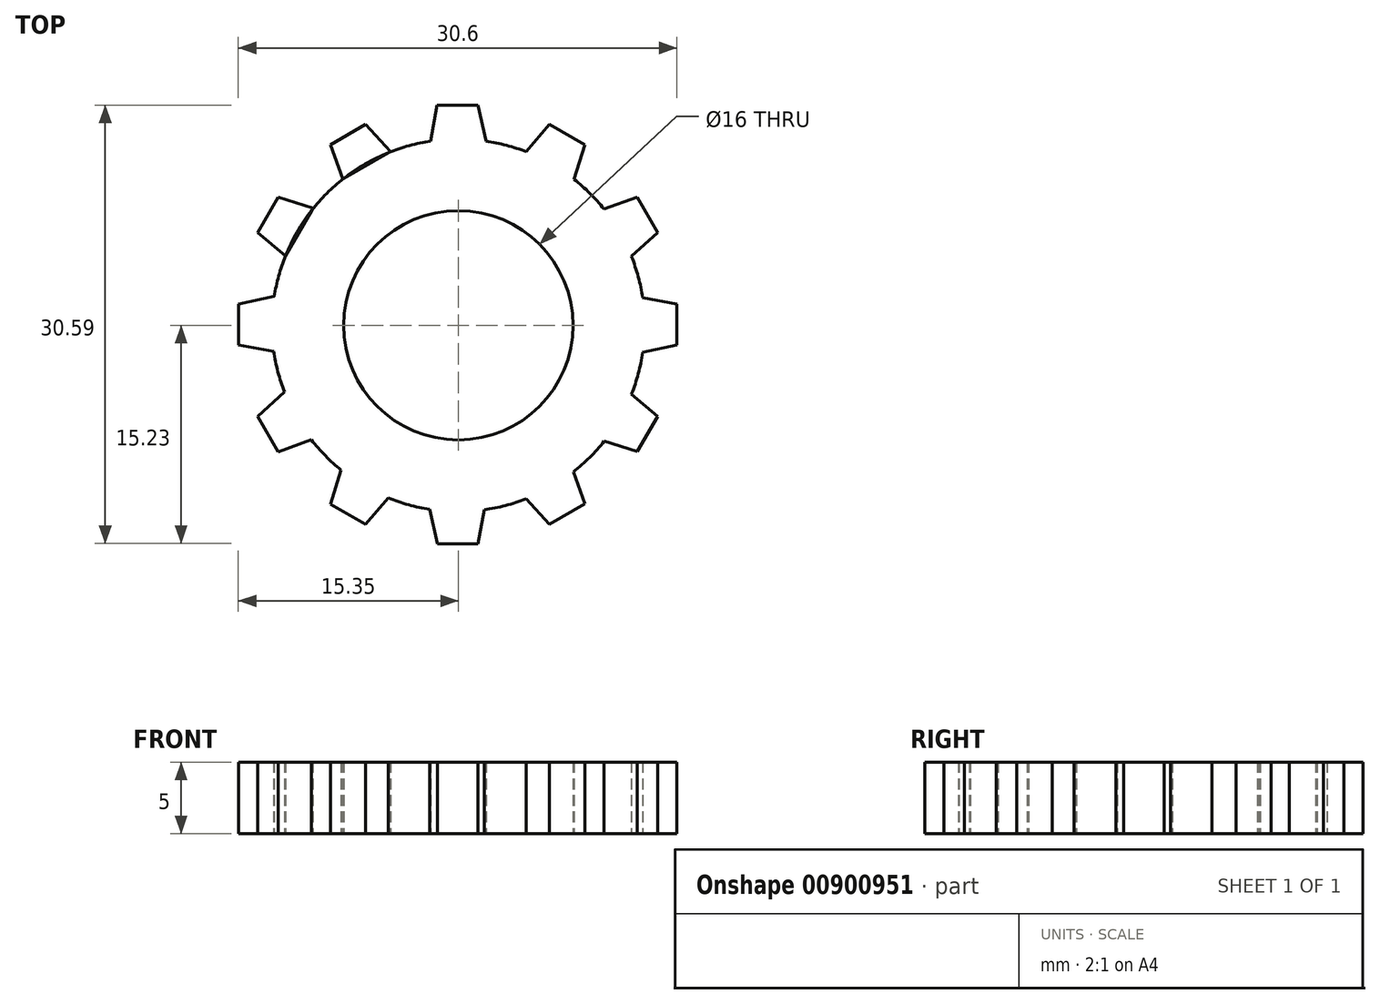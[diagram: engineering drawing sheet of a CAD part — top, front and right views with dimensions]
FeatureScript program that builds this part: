
annotation { "Feature Type Name" : "Feature", "Feature Type Description" : "" }
export const myFeature = defineFeature(function(context is Context, id is Id, definition is map)
    precondition{}
    {
        {
            var Q0;
            Q0=qCreatedBy(makeId("Top.planeOp"),FACE);
            var sketch = newSketch(context, id + "F0", { "sketchPlane" : qUnion([Q0])});
            skCircle(sketch, "E0", {"center": v(0, 0) * mm, "radius": 13 * mm});
            skLineSegment(sketch, "E1", {"start": v(-1.92, 12.86) * mm, "end": v(1.93, 12.86) * mm});
            skLineSegment(sketch, "E2", {"start": v(1.93, 12.86) * mm, "end": v(1.37, 15.36) * mm});
            skLineSegment(sketch, "E3", {"start": v(1.37, 15.36) * mm, "end": v(-1.48, 15.36) * mm});
            skLineSegment(sketch, "E4", {"start": v(-1.48, 15.36) * mm, "end": v(-1.92, 12.86) * mm});
            skLineSegment(sketch, "E5.1.0", {"start": v(-6.47, 14.02) * mm, "end": v(-8.93, 12.6) * mm});
            skLineSegment(sketch, "E5.1.1", {"start": v(-4.74, 12.13) * mm, "end": v(-6.47, 14.02) * mm});
            skLineSegment(sketch, "E5.1.2", {"start": v(-8.07, 10.2) * mm, "end": v(-4.74, 12.13) * mm});
            skLineSegment(sketch, "E5.1.3", {"start": v(-8.93, 12.6) * mm, "end": v(-8.07, 10.2) * mm});
            skLineSegment(sketch, "E5.2.0", {"start": v(-12.58, 8.94) * mm, "end": v(-14, 6.47) * mm});
            skLineSegment(sketch, "E5.2.1", {"start": v(-10.14, 8.17) * mm, "end": v(-12.58, 8.94) * mm});
            skLineSegment(sketch, "E5.2.2", {"start": v(-12.07, 4.83) * mm, "end": v(-10.14, 8.17) * mm});
            skLineSegment(sketch, "E5.2.3", {"start": v(-14, 6.47) * mm, "end": v(-12.07, 4.83) * mm});
            skPoint(sketch, "E5.center", {"position": v(-0.05, 0.06) * mm});
            skLineSegment(sketch, "E6.2.3.0", {"start": v(-15.35, 1.48) * mm, "end": v(-15.35, -1.37) * mm});
            skLineSegment(sketch, "E6.3.3.0", {"start": v(-12.85, 2.04) * mm, "end": v(-15.35, 1.48) * mm});
            skLineSegment(sketch, "E6.6.3.0", {"start": v(-12.85, -1.81) * mm, "end": v(-12.85, 2.04) * mm});
            skLineSegment(sketch, "E6.9.3.0", {"start": v(-15.35, -1.37) * mm, "end": v(-12.85, -1.81) * mm});
            skLineSegment(sketch, "E6.2.4.0", {"start": v(-14, -6.35) * mm, "end": v(-12.58, -8.82) * mm});
            skLineSegment(sketch, "E6.3.4.0", {"start": v(-12.12, -4.63) * mm, "end": v(-14, -6.35) * mm});
            skLineSegment(sketch, "E6.6.4.0", {"start": v(-10.2, -7.96) * mm, "end": v(-12.12, -4.63) * mm});
            skLineSegment(sketch, "E6.9.4.0", {"start": v(-12.58, -8.82) * mm, "end": v(-10.2, -7.96) * mm});
            skLineSegment(sketch, "E6.2.5.0", {"start": v(-8.93, -12.47) * mm, "end": v(-6.46, -13.9) * mm});
            skLineSegment(sketch, "E6.3.5.0", {"start": v(-8.16, -10.03) * mm, "end": v(-8.93, -12.47) * mm});
            skLineSegment(sketch, "E6.6.5.0", {"start": v(-4.82, -11.96) * mm, "end": v(-8.16, -10.03) * mm});
            skLineSegment(sketch, "E6.9.5.0", {"start": v(-6.46, -13.9) * mm, "end": v(-4.82, -11.96) * mm});
            skLineSegment(sketch, "E6.2.6.0", {"start": v(-1.47, -15.23) * mm, "end": v(1.38, -15.23) * mm});
            skLineSegment(sketch, "E6.3.6.0", {"start": v(-2.02, -12.73) * mm, "end": v(-1.47, -15.23) * mm});
            skLineSegment(sketch, "E6.6.6.0", {"start": v(1.83, -12.73) * mm, "end": v(-2.02, -12.73) * mm});
            skLineSegment(sketch, "E6.9.6.0", {"start": v(1.38, -15.23) * mm, "end": v(1.83, -12.73) * mm});
            skLineSegment(sketch, "E6.2.7.0", {"start": v(6.37, -13.9) * mm, "end": v(8.83, -12.47) * mm});
            skLineSegment(sketch, "E6.3.7.0", {"start": v(4.64, -12) * mm, "end": v(6.37, -13.9) * mm});
            skLineSegment(sketch, "E6.6.7.0", {"start": v(7.97, -10.08) * mm, "end": v(4.64, -12) * mm});
            skLineSegment(sketch, "E6.9.7.0", {"start": v(8.83, -12.47) * mm, "end": v(7.97, -10.08) * mm});
            skLineSegment(sketch, "E6.2.8.0", {"start": v(12.49, -8.82) * mm, "end": v(13.91, -6.35) * mm});
            skLineSegment(sketch, "E6.3.8.0", {"start": v(10.04, -8.05) * mm, "end": v(12.49, -8.82) * mm});
            skLineSegment(sketch, "E6.6.8.0", {"start": v(11.97, -4.71) * mm, "end": v(10.04, -8.05) * mm});
            skLineSegment(sketch, "E6.9.8.0", {"start": v(13.91, -6.35) * mm, "end": v(11.97, -4.71) * mm});
            skLineSegment(sketch, "E6.2.9.0", {"start": v(15.25, -1.36) * mm, "end": v(15.25, 1.49) * mm});
            skLineSegment(sketch, "E6.3.9.0", {"start": v(12.75, -1.91) * mm, "end": v(15.25, -1.36) * mm});
            skLineSegment(sketch, "E6.6.9.0", {"start": v(12.75, 1.94) * mm, "end": v(12.75, -1.91) * mm});
            skLineSegment(sketch, "E6.9.9.0", {"start": v(15.25, 1.49) * mm, "end": v(12.75, 1.94) * mm});
            skLineSegment(sketch, "E6.2.10.0", {"start": v(13.9, 6.48) * mm, "end": v(12.48, 8.95) * mm});
            skLineSegment(sketch, "E6.3.10.0", {"start": v(12.02, 4.75) * mm, "end": v(13.9, 6.48) * mm});
            skLineSegment(sketch, "E6.6.10.0", {"start": v(10.1, 8.08) * mm, "end": v(12.02, 4.75) * mm});
            skLineSegment(sketch, "E6.9.10.0", {"start": v(12.48, 8.95) * mm, "end": v(10.1, 8.08) * mm});
            skLineSegment(sketch, "E6.2.11.0", {"start": v(8.83, 12.6) * mm, "end": v(6.36, 14.02) * mm});
            skLineSegment(sketch, "E6.3.11.0", {"start": v(8.06, 10.16) * mm, "end": v(8.83, 12.6) * mm});
            skLineSegment(sketch, "E6.6.11.0", {"start": v(4.72, 12.08) * mm, "end": v(8.06, 10.16) * mm});
            skLineSegment(sketch, "E6.9.11.0", {"start": v(6.36, 14.02) * mm, "end": v(4.72, 12.08) * mm});
            skCircle(sketch, "E7", {"center": v(0, 0) * mm, "radius": 8 * mm});
            skSolve(sketch);
        }
        {
            var Q0;
            Q0=makeQuery(id+"F0.imprint","IMPRINT",FACE,{"disambiguationData":[TD([[makeQuery(id+"F0.imprint","IMPRINT",EDGE,{"derivedFrom":sQuery(id+"F0.wireOp",EDGE,"E5.1.0")}),1.0]])]});
            var Q1;
            {var subQ8=sQuery(id+"F0.wireOp",EDGE,"E1");Q1=makeQuery(id+"F0.imprint","IMPRINT",FACE,{"disambiguationData":[TD([[makeQuery(id+"F0.imprint","IMPRINT",EDGE,{"derivedFrom":subQ8}),-1.0]])]});}
            var Q2;
            Q2=makeQuery(id+"F0.imprint","IMPRINT",FACE,{"disambiguationData":[TD([[makeQuery(id+"F0.imprint","IMPRINT",EDGE,{"derivedFrom":sQuery(id+"F0.wireOp",EDGE,"E5.2.0")}),1.0]])]});
            var Q3;
            {var subQ4=sQuery(id+"F0.wireOp",EDGE,"E6.2.3.0");Q3=makeQuery(id+"F0.imprint","IMPRINT",FACE,{"disambiguationData":[TD([[makeQuery(id+"F0.imprint","IMPRINT",EDGE,{"derivedFrom":subQ4}),1.0]])]});}
            var Q4;
            {var subQ5=sQuery(id+"F0.wireOp",EDGE,"E6.2.4.0");Q4=makeQuery(id+"F0.imprint","IMPRINT",FACE,{"disambiguationData":[TD([[makeQuery(id+"F0.imprint","IMPRINT",EDGE,{"derivedFrom":subQ5}),1.0]])]});}
            var Q5;
            {var subQ5=sQuery(id+"F0.wireOp",EDGE,"E6.2.5.0");Q5=makeQuery(id+"F0.imprint","IMPRINT",FACE,{"disambiguationData":[TD([[makeQuery(id+"F0.imprint","IMPRINT",EDGE,{"derivedFrom":subQ5}),1.0]])]});}
            var Q6;
            {var subQ5=sQuery(id+"F0.wireOp",EDGE,"E6.2.6.0");Q6=makeQuery(id+"F0.imprint","IMPRINT",FACE,{"disambiguationData":[TD([[makeQuery(id+"F0.imprint","IMPRINT",EDGE,{"derivedFrom":subQ5}),1.0]])]});}
            var Q7;
            {var subQ5=sQuery(id+"F0.wireOp",EDGE,"E6.2.7.0");Q7=makeQuery(id+"F0.imprint","IMPRINT",FACE,{"disambiguationData":[TD([[makeQuery(id+"F0.imprint","IMPRINT",EDGE,{"derivedFrom":subQ5}),1.0]])]});}
            var Q8;
            {var subQ5=sQuery(id+"F0.wireOp",EDGE,"E6.2.8.0");Q8=makeQuery(id+"F0.imprint","IMPRINT",FACE,{"disambiguationData":[TD([[makeQuery(id+"F0.imprint","IMPRINT",EDGE,{"derivedFrom":subQ5}),1.0]])]});}
            var Q9;
            {var subQ5=sQuery(id+"F0.wireOp",EDGE,"E6.2.9.0");Q9=makeQuery(id+"F0.imprint","IMPRINT",FACE,{"disambiguationData":[TD([[makeQuery(id+"F0.imprint","IMPRINT",EDGE,{"derivedFrom":subQ5}),1.0]])]});}
            var Q10;
            {var subQ5=sQuery(id+"F0.wireOp",EDGE,"E6.2.11.0");Q10=makeQuery(id+"F0.imprint","IMPRINT",FACE,{"disambiguationData":[TD([[makeQuery(id+"F0.imprint","IMPRINT",EDGE,{"derivedFrom":subQ5}),1.0]])]});}
            var Q11;
            {var subQ3=sQuery(id+"F0.wireOp",EDGE,"E2");Q11=makeQuery(id+"F0.imprint","IMPRINT",FACE,{"disambiguationData":[TD([[makeQuery(id+"F0.imprint","IMPRINT",EDGE,{"derivedFrom":subQ3}),1.0]])]});}
            var Q12;
            {var subQ5=sQuery(id+"F0.wireOp",EDGE,"E6.2.10.0");Q12=makeQuery(id+"F0.imprint","IMPRINT",FACE,{"disambiguationData":[TD([[makeQuery(id+"F0.imprint","IMPRINT",EDGE,{"derivedFrom":subQ5}),1.0]])]});}
            var Q13;
            {var subQ5=sQuery(id+"F0.wireOp",EDGE,"E6.6.9.0");Q13=makeQuery(id+"F0.imprint","IMPRINT",FACE,{"disambiguationData":[TD([[makeQuery(id+"F0.imprint","IMPRINT",EDGE,{"derivedFrom":subQ5}),1.0]])]});}
            var Q14;
            {var subQ5=sQuery(id+"F0.wireOp",EDGE,"E6.6.10.0");Q14=makeQuery(id+"F0.imprint","IMPRINT",FACE,{"disambiguationData":[TD([[makeQuery(id+"F0.imprint","IMPRINT",EDGE,{"derivedFrom":subQ5}),1.0]])]});}
            var Q15;
            {var subQ5=sQuery(id+"F0.wireOp",EDGE,"E6.6.11.0");Q15=makeQuery(id+"F0.imprint","IMPRINT",FACE,{"disambiguationData":[TD([[makeQuery(id+"F0.imprint","IMPRINT",EDGE,{"derivedFrom":subQ5}),1.0]])]});}
            var Q16;
            {var subQ0=sQuery(id+"F0.wireOp",EDGE,"E1");Q16=makeQuery(id+"F0.imprint","IMPRINT",FACE,{"disambiguationData":[TD([[makeQuery(id+"F0.imprint","IMPRINT",EDGE,{"derivedFrom":subQ0}),1.0]])]});}
            var Q17;
            {var subQ0=sQuery(id+"F0.wireOp",EDGE,"E5.1.2");var subQ1=sQuery(id+"F0.wireOp",EDGE,"E0");var subQ2=makeQuery(id+"F0.imprint","INTERSECT",VERTEX,{"disambiguationData":[OD(0.0)],"derivedFrom":[subQ1,subQ0]});Q17=makeQuery(id+"F0.imprint","IMPRINT",FACE,{"disambiguationData":[TD([[makeQuery(id+"F0.imprint","IMPRINT",EDGE,{"disambiguationData":[TD([[subQ2,-1.0]])],"derivedFrom":subQ1}),1.0]])]});}
            var Q18;
            {var subQ0=sQuery(id+"F0.wireOp",EDGE,"E5.2.2");var subQ1=sQuery(id+"F0.wireOp",EDGE,"E0");var subQ2=makeQuery(id+"F0.imprint","INTERSECT",VERTEX,{"disambiguationData":[OD(0.0)],"derivedFrom":[subQ1,subQ0]});Q18=makeQuery(id+"F0.imprint","IMPRINT",FACE,{"disambiguationData":[TD([[makeQuery(id+"F0.imprint","IMPRINT",EDGE,{"disambiguationData":[TD([[subQ2,-1.0]])],"derivedFrom":subQ1}),1.0]])]});}
            var Q19;
            {var subQ0=sQuery(id+"F0.wireOp",EDGE,"E6.6.3.0");var subQ1=sQuery(id+"F0.wireOp",EDGE,"E0");var subQ2=makeQuery(id+"F0.imprint","INTERSECT",VERTEX,{"derivedFrom":[subQ1,subQ0]});Q19=makeQuery(id+"F0.imprint","IMPRINT",FACE,{"disambiguationData":[TD([[makeQuery(id+"F0.imprint","IMPRINT",EDGE,{"disambiguationData":[TD([[subQ2,-1.0]])],"derivedFrom":subQ1}),1.0]])]});}
            var Q20;
            {var subQ5=sQuery(id+"F0.wireOp",EDGE,"E6.6.4.0");Q20=makeQuery(id+"F0.imprint","IMPRINT",FACE,{"disambiguationData":[TD([[makeQuery(id+"F0.imprint","IMPRINT",EDGE,{"derivedFrom":subQ5}),1.0]])]});}
            var Q21;
            {var subQ5=sQuery(id+"F0.wireOp",EDGE,"E6.6.5.0");Q21=makeQuery(id+"F0.imprint","IMPRINT",FACE,{"disambiguationData":[TD([[makeQuery(id+"F0.imprint","IMPRINT",EDGE,{"derivedFrom":subQ5}),1.0]])]});}
            var Q22;
            {var subQ5=sQuery(id+"F0.wireOp",EDGE,"E6.6.6.0");Q22=makeQuery(id+"F0.imprint","IMPRINT",FACE,{"disambiguationData":[TD([[makeQuery(id+"F0.imprint","IMPRINT",EDGE,{"derivedFrom":subQ5}),1.0]])]});}
            var Q23;
            {var subQ5=sQuery(id+"F0.wireOp",EDGE,"E6.6.7.0");Q23=makeQuery(id+"F0.imprint","IMPRINT",FACE,{"disambiguationData":[TD([[makeQuery(id+"F0.imprint","IMPRINT",EDGE,{"derivedFrom":subQ5}),1.0]])]});}
            var Q24;
            {var subQ5=sQuery(id+"F0.wireOp",EDGE,"E6.6.8.0");Q24=makeQuery(id+"F0.imprint","IMPRINT",FACE,{"disambiguationData":[TD([[makeQuery(id+"F0.imprint","IMPRINT",EDGE,{"derivedFrom":subQ5}),1.0]])]});}
            extrude(context, id + "F1", {"entities" : qUnion([Q0, Q1, Q2, Q3, Q4, Q5, Q6, Q7, Q8, Q9, Q10, Q11, Q12, Q13, Q14, Q15, Q16, Q17, Q18, Q19, Q20, Q21, Q22, Q23, Q24]), "depth" : 5 * mm, "offsetDistance" : 25 * mm});
        }
    });
